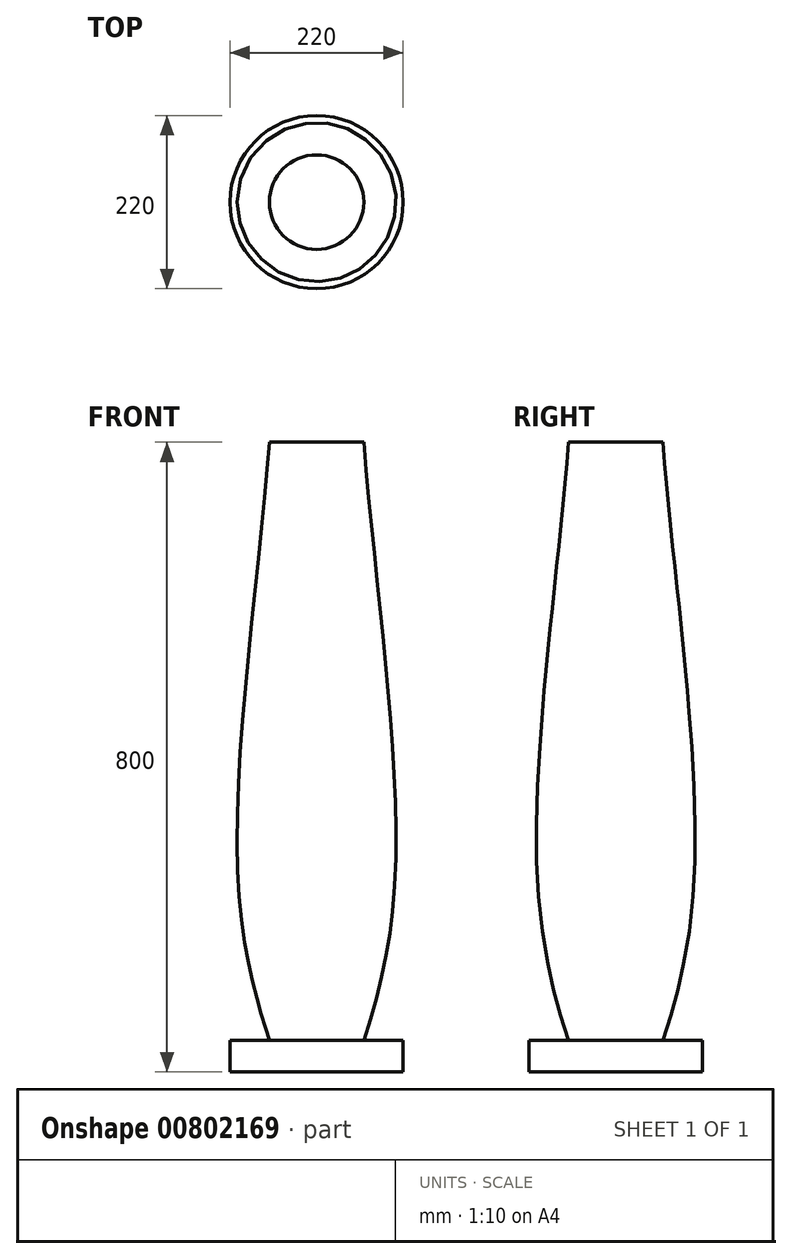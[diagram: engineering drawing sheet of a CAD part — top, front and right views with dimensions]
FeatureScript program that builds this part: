
annotation { "Feature Type Name" : "Feature", "Feature Type Description" : "" }
export const myFeature = defineFeature(function(context is Context, id is Id, definition is map)
    precondition{}
    {
        {
            var Q0;
            Q0=qCreatedBy(makeId("Front.planeOp"),FACE);
            var sketch = newSketch(context, id + "F0", { "sketchPlane" : qUnion([Q0])});
            skLineSegment(sketch, "E0", {"start": v(0, -380.3) * mm, "end": v(0, 419.7) * mm});
            skLineSegment(sketch, "E1", {"start": v(0, -380.3) * mm, "end": v(-110, -380.3) * mm});
            skLineSegment(sketch, "E2", {"start": v(-110, -380.3) * mm, "end": v(-110, -340.3) * mm});
            skLineSegment(sketch, "E3", {"start": v(-110, -340.3) * mm, "end": v(-60, -340.3) * mm});
            skFitSpline(sketch, "E4", {"points": [v(-60, -340.3) * mm, v(-100, -130.3) * mm, v(-60, 419.7) * mm], "startDerivative": vector(-110.26, 343.44) * mm, "endDerivative": vector(55.71, 761.52) * mm});
            skLineSegment(sketch, "E5", {"start": v(-60, 419.7) * mm, "end": v(0, 419.7) * mm});
            skSolve(sketch);
        }
        {
            var Q0;
            Q0=qCreatedBy(makeId("Front.planeOp"),FACE);
            var sketch = newSketch(context, id + "F1", { "sketchPlane" : qUnion([Q0])});
            skLineSegment(sketch, "E6", {"start": v(0, -544.04) * mm, "end": v(0, 661.06) * mm, "construction": true});
            skSolve(sketch);
        }
        {
            var Q0;
            Q0 = qSketchRegion(id + "F0", true);
            var Q1;
            Q1=sQuery(id+"F1.wireOp",EDGE,"E6");
            revolve(context, id + "F2", {"surfaceOperationType" : NewSurfaceOperationType.NEW, "entities" : qUnion([Q0]), "axis" : qUnion([Q1]), "revolveType" : RevolveType.FULL});
        }
    });
